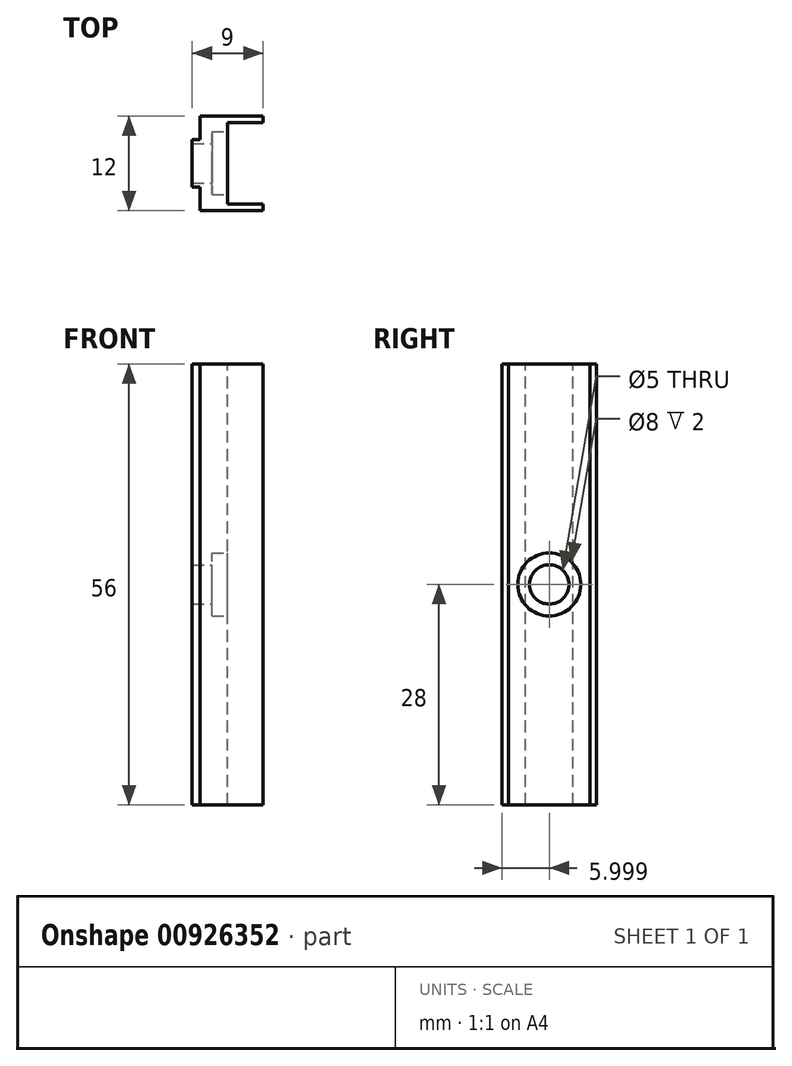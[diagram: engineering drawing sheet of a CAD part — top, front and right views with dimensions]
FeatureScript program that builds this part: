
annotation { "Feature Type Name" : "Feature", "Feature Type Description" : "" }
export const myFeature = defineFeature(function(context is Context, id is Id, definition is map)
    precondition{}
    {
        {
            var Q0;
            Q0=qCreatedBy(makeId("Top.planeOp"),FACE);
            var sketch = newSketch(context, id + "F0", { "sketchPlane" : qUnion([Q0])});
            skLineSegment(sketch, "E0", {"start": v(-67.44, 14.7) * mm, "end": v(-59.44, 14.7) * mm});
            skLineSegment(sketch, "E1", {"start": v(-59.44, 14.7) * mm, "end": v(-59.44, 2.7) * mm});
            skLineSegment(sketch, "E2", {"start": v(-59.44, 2.7) * mm, "end": v(-67.44, 2.7) * mm});
            skLineSegment(sketch, "E3", {"start": v(-67.44, 2.7) * mm, "end": v(-67.44, 14.7) * mm});
            skSolve(sketch);
        }
        {
            var Q0;
            Q0=makeQuery(id+"F0.imprint","IMPRINT",FACE,{"disambiguationData":[TD([[makeQuery(id+"F0.imprint","IMPRINT",EDGE,{"derivedFrom":sQuery(id+"F0.wireOp",EDGE,"E0")}),-1.0]])]});
            extrude(context, id + "F1", {"entities" : qUnion([Q0]), "depth" : 56 * mm, "offsetDistance" : 25 * mm});
        }
        {
            var Q0;
            Q0=makeQuery(id+"F1.opExtrude","CAP_FACE",FACE,{"disambiguationData":[OSD([sQuery(id+"F0.wireOp",EDGE,"E0"),sQuery(id+"F0.wireOp",EDGE,"E1"),sQuery(id+"F0.wireOp",EDGE,"E2"),sQuery(id+"F0.wireOp",EDGE,"E3")])],"isStart":false});
            var sketch = newSketch(context, id + "F2", { "sketchPlane" : qUnion([Q0])});
            skLineSegment(sketch, "E4", {"start": v(-59.44, 14.7) * mm, "end": v(-59.44, 13.9) * mm});
            skLineSegment(sketch, "E5", {"start": v(-59.44, 13.9) * mm, "end": v(-64.44, 13.9) * mm});
            skLineSegment(sketch, "E6", {"start": v(-64.44, 13.9) * mm, "end": v(-64.44, 3.5) * mm});
            skLineSegment(sketch, "E7", {"start": v(-64.44, 3.5) * mm, "end": v(-59.44, 3.5) * mm});
            skSolve(sketch);
        }
        {
            var Q0;
            {var subQ0=sQuery(id+"F2.wireOp",EDGE,"E5");Q0=makeQuery(id+"F2.imprint","IMPRINT",FACE,{"disambiguationData":[TD([[makeQuery(id+"F2.imprint","IMPRINT",EDGE,{"derivedFrom":subQ0}),1.0]])]});}
            extrude(context, id + "F3", {"entities" : qUnion([Q0]), "operationType" : NewBodyOperationType.REMOVE, "oppositeDirection" : true, "depth" : 56 * mm, "offsetDistance" : 25 * mm});
        }
        {
            var Q0;
            Q0=makeQuery(id+"F1.opExtrude","CAP_FACE",FACE,{"disambiguationData":[OSD([sQuery(id+"F0.wireOp",EDGE,"E0"),sQuery(id+"F0.wireOp",EDGE,"E1"),sQuery(id+"F0.wireOp",EDGE,"E2"),sQuery(id+"F0.wireOp",EDGE,"E3")])],"isStart":false});
            var sketch = newSketch(context, id + "F4", { "sketchPlane" : qUnion([Q0])});
            skLineSegment(sketch, "E8", {"start": v(-67.44, 8.7) * mm, "end": v(-67.44, 11.7) * mm});
            skLineSegment(sketch, "E9", {"start": v(-67.44, 11.7) * mm, "end": v(-68.44, 11.7) * mm});
            skLineSegment(sketch, "E10", {"start": v(-68.44, 11.7) * mm, "end": v(-68.44, 5.7) * mm});
            skLineSegment(sketch, "E11", {"start": v(-68.44, 5.7) * mm, "end": v(-67.44, 5.7) * mm});
            skSolve(sketch);
        }
        {
            var Q0;
            {var subQ1=sQuery(id+"F4.wireOp",EDGE,"E8");Q0=makeQuery(id+"F4.imprint","IMPRINT",FACE,{"disambiguationData":[TD([[makeQuery(id+"F4.imprint","IMPRINT",EDGE,{"derivedFrom":subQ1}),1.0]])]});}
            extrude(context, id + "F5", {"entities" : qUnion([Q0]), "operationType" : NewBodyOperationType.ADD, "oppositeDirection" : true, "depth" : 56 * mm, "offsetDistance" : 25 * mm});
        }
        {
            var Q0;
            Q0=makeQuery(id+"F3.boolean.opBoolean","COPY",FACE,{"derivedFrom":makeQuery(id+"F3.opExtrude","SWEPT_FACE",FACE,{"disambiguationData":[OSD([sQuery(id+"F2.wireOp",EDGE,"E6")])]})});
            var sketch = newSketch(context, id + "F6", { "sketchPlane" : qUnion([Q0])});
            skLineSegment(sketch, "E12", {"start": v(13.9, 28) * mm, "end": v(3.5, 28) * mm});
            skLineSegment(sketch, "E13", {"start": v(8.7, 28) * mm, "end": v(8.7, 32.49) * mm});
            skSolve(sketch);
        }
        {
            var Q0;
            Q0=sQuery(id+"F6.wireOp",VERTEX,"E13.start");
            var Q1;
            Q1=makeQuery(id+"F1.opExtrude","SWEPT_BODY",BODY,{"disambiguationData":[OSD([sQuery(id+"F0.wireOp",EDGE,"E0"),sQuery(id+"F0.wireOp",EDGE,"E1"),sQuery(id+"F0.wireOp",EDGE,"E2"),sQuery(id+"F0.wireOp",EDGE,"E3")])]});
            hole(context, id + "F7", {"style" : HoleStyle.C_BORE, "endStyle" : HoleEndStyle.BLIND, "holeDiameter" : 5 * mm, "cBoreDiameter" : 8 * mm, "cBoreDepth" : 1.5 * mm, "majorDiameter" : 5 * mm, "holeDepth" : 34 * mm, "isTappedThrough" : true, "tappedDepth" : 8.5 * mm, "tapClearance" : 3, "startFromSketch" : true, "locations" : qUnion([Q0]), "scope" : qUnion([Q1])});
        }
        {
            var Q0;
            Q0=makeQuery(id+"F3.boolean.opBoolean","COPY",FACE,{"derivedFrom":makeQuery(id+"F3.opExtrude","SWEPT_FACE",FACE,{"disambiguationData":[OSD([sQuery(id+"F2.wireOp",EDGE,"E6")])]})});
            extrude(context, id + "F8", {"entities" : qUnion([Q0]), "operationType" : NewBodyOperationType.ADD, "depth" : 0.5 * mm, "offsetDistance" : 25 * mm});
        }
    });
